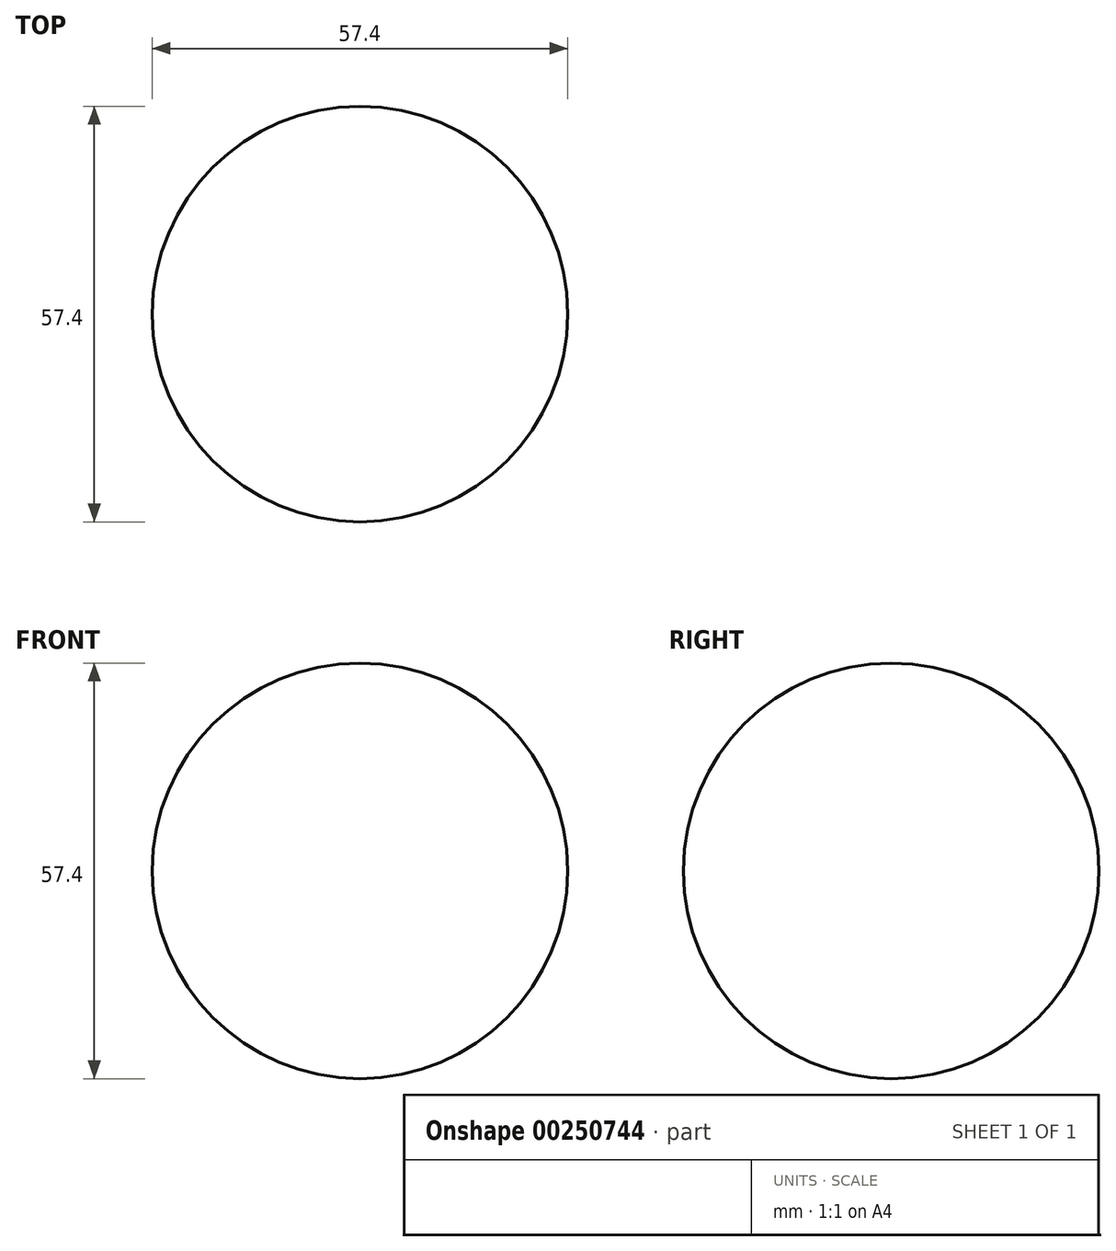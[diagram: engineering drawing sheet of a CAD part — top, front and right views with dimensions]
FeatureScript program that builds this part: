
annotation { "Feature Type Name" : "Feature", "Feature Type Description" : "" }
export const myFeature = defineFeature(function(context is Context, id is Id, definition is map)
    precondition{}
    {
        {
            var Q0;
            Q0=qCreatedBy(makeId("Front.planeOp"),FACE);
            var sketch = newSketch(context, id + "F0", { "sketchPlane" : qUnion([Q0])});
            skLineSegment(sketch, "E0", {"start": v(0, 0) * mm, "end": v(0, 57.4) * mm});
            skArc(sketch, "E1", {"start": v(0, 57.4) * mm, "mid": v(28.7, 28.7) * mm, "end": v(0, 0) * mm});
            skSolve(sketch);
        }
        {
            var Q0;
            Q0 = qSketchRegion(id + "F0", true);
            var Q1;
            Q1=sQuery(id+"F0.wireOp",EDGE,"E0");
            revolve(context, id + "F1", {"entities" : qUnion([Q0]), "axis" : qUnion([Q1]), "revolveType" : RevolveType.FULL});
        }
    });
